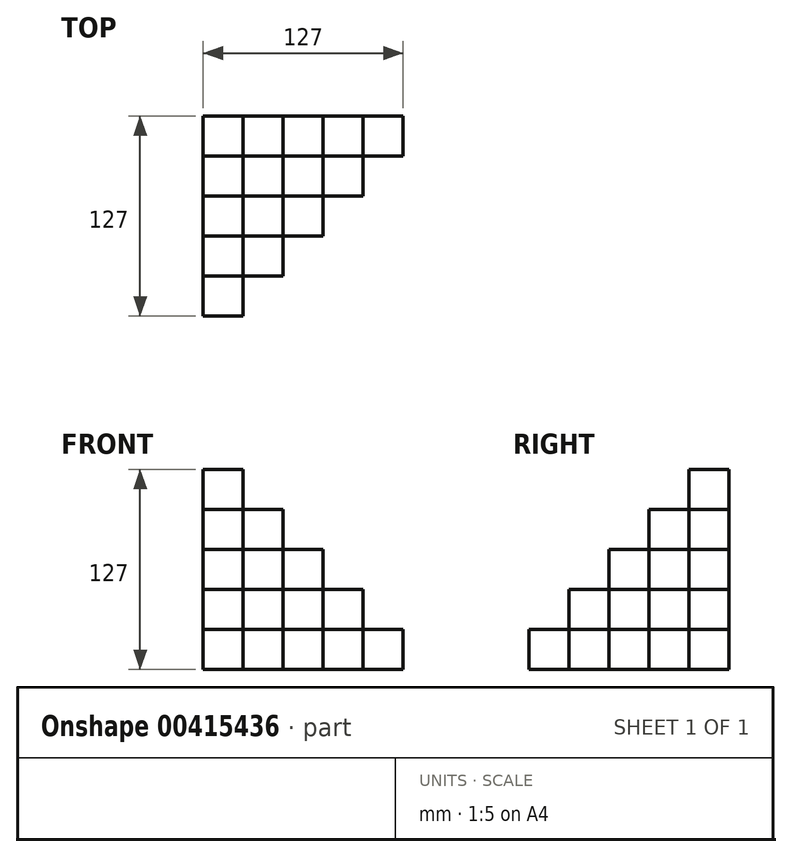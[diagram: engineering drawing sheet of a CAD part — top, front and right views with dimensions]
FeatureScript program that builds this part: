
annotation { "Feature Type Name" : "Feature", "Feature Type Description" : "" }
export const myFeature = defineFeature(function(context is Context, id is Id, definition is map)
    precondition{}
    {
        {
            var Q0;
            Q0=qCreatedBy(makeId("Top.planeOp"),FACE);
            var sketch = newSketch(context, id + "F0", { "sketchPlane" : qUnion([Q0])});
            skLineSegment(sketch, "E0.bottom", {"start": v(63.5, 63.5) * mm, "end": v(-63.5, 63.5) * mm, "construction": true});
            skLineSegment(sketch, "E0.top", {"start": v(63.5, -63.5) * mm, "end": v(-63.5, -63.5) * mm, "construction": true});
            skLineSegment(sketch, "E0.left", {"start": v(63.5, 63.5) * mm, "end": v(63.5, -63.5) * mm, "construction": true});
            skLineSegment(sketch, "E0.right", {"start": v(-63.5, 63.5) * mm, "end": v(-63.5, -63.5) * mm, "construction": true});
            skPoint(sketch, "E0.middle", {"position": v(0, 0) * mm});
            skLineSegment(sketch, "E1.bottom", {"start": v(-63.5, -63.5) * mm, "end": v(-38.1, -63.5) * mm});
            skLineSegment(sketch, "E1.top", {"start": v(-63.5, -38.1) * mm, "end": v(-38.1, -38.1) * mm});
            skLineSegment(sketch, "E1.left", {"start": v(-63.5, -63.5) * mm, "end": v(-63.5, -38.1) * mm});
            skLineSegment(sketch, "E1.right", {"start": v(-38.1, -63.5) * mm, "end": v(-38.1, -38.1) * mm});
            skLineSegment(sketch, "E2.bottom", {"start": v(-38.1, -38.1) * mm, "end": v(-12.7, -38.1) * mm});
            skLineSegment(sketch, "E2.top", {"start": v(-38.1, -12.7) * mm, "end": v(-12.7, -12.7) * mm});
            skLineSegment(sketch, "E2.left", {"start": v(-38.1, -38.1) * mm, "end": v(-38.1, -12.7) * mm});
            skLineSegment(sketch, "E2.right", {"start": v(-12.7, -38.1) * mm, "end": v(-12.7, -12.7) * mm});
            skLineSegment(sketch, "E3.bottom", {"start": v(-12.7, -12.7) * mm, "end": v(12.7, -12.7) * mm});
            skLineSegment(sketch, "E3.top", {"start": v(-12.7, 12.7) * mm, "end": v(12.7, 12.7) * mm});
            skLineSegment(sketch, "E3.left", {"start": v(-12.7, -12.7) * mm, "end": v(-12.7, 12.7) * mm});
            skLineSegment(sketch, "E3.right", {"start": v(12.7, -12.7) * mm, "end": v(12.7, 12.7) * mm});
            skLineSegment(sketch, "E4.bottom", {"start": v(12.7, 12.7) * mm, "end": v(38.1, 12.7) * mm});
            skLineSegment(sketch, "E4.top", {"start": v(12.7, 38.1) * mm, "end": v(38.1, 38.1) * mm});
            skLineSegment(sketch, "E4.left", {"start": v(12.7, 12.7) * mm, "end": v(12.7, 38.1) * mm});
            skLineSegment(sketch, "E4.right", {"start": v(38.1, 12.7) * mm, "end": v(38.1, 38.1) * mm});
            skLineSegment(sketch, "E5.bottom", {"start": v(38.1, 38.1) * mm, "end": v(63.5, 38.1) * mm});
            skLineSegment(sketch, "E5.top", {"start": v(38.1, 63.5) * mm, "end": v(63.5, 63.5) * mm});
            skLineSegment(sketch, "E5.left", {"start": v(38.1, 38.1) * mm, "end": v(38.1, 63.5) * mm});
            skLineSegment(sketch, "E5.right", {"start": v(63.5, 38.1) * mm, "end": v(63.5, 63.5) * mm});
            skSolve(sketch);
        }
        {
            var Q0;
            Q0=makeQuery(id+"F0.imprint","IMPRINT",FACE,{"disambiguationData":[TD([[makeQuery(id+"F0.imprint","IMPRINT",EDGE,{"derivedFrom":sQuery(id+"F0.wireOp",EDGE,"E2.bottom")}),1.0]])]});
            var Q1;
            Q1=makeQuery(id+"F0.imprint","IMPRINT",FACE,{"disambiguationData":[TD([[makeQuery(id+"F0.imprint","IMPRINT",EDGE,{"derivedFrom":sQuery(id+"F0.wireOp",EDGE,"E1.bottom")}),1.0]])]});
            var Q2;
            Q2=makeQuery(id+"F0.imprint","IMPRINT",FACE,{"disambiguationData":[TD([[makeQuery(id+"F0.imprint","IMPRINT",EDGE,{"derivedFrom":sQuery(id+"F0.wireOp",EDGE,"E3.bottom")}),1.0]])]});
            var Q3;
            Q3=makeQuery(id+"F0.imprint","IMPRINT",FACE,{"disambiguationData":[TD([[makeQuery(id+"F0.imprint","IMPRINT",EDGE,{"derivedFrom":sQuery(id+"F0.wireOp",EDGE,"E4.bottom")}),1.0]])]});
            var Q4;
            Q4=makeQuery(id+"F0.imprint","IMPRINT",FACE,{"disambiguationData":[TD([[makeQuery(id+"F0.imprint","IMPRINT",EDGE,{"derivedFrom":sQuery(id+"F0.wireOp",EDGE,"E5.bottom")}),1.0]])]});
            extrude(context, id + "F1", {"entities" : qUnion([Q0, Q1, Q2, Q3, Q4]), "depth" : 25.4 * mm});
        }
        {
            var Q0;
            Q0=qCreatedBy(makeId("Top.planeOp"),FACE);
            var sketch = newSketch(context, id + "F2", { "sketchPlane" : qUnion([Q0])});
            skLineSegment(sketch, "E6.bottom", {"start": v(63.5, 63.5) * mm, "end": v(-63.5, 63.5) * mm, "construction": true});
            skLineSegment(sketch, "E6.top", {"start": v(63.5, -63.5) * mm, "end": v(-63.5, -63.5) * mm, "construction": true});
            skLineSegment(sketch, "E6.left", {"start": v(63.5, 63.5) * mm, "end": v(63.5, -63.5) * mm, "construction": true});
            skLineSegment(sketch, "E6.right", {"start": v(-63.5, 63.5) * mm, "end": v(-63.5, -63.5) * mm, "construction": true});
            skPoint(sketch, "E6.middle", {"position": v(0, 0) * mm});
            skLineSegment(sketch, "E7", {"start": v(-63.5, -63.5) * mm, "end": v(-63.5, -38.1) * mm, "construction": true});
            skLineSegment(sketch, "E8", {"start": v(63.5, 63.5) * mm, "end": v(38.1, 63.5) * mm, "construction": true});
            skLineSegment(sketch, "E9.bottom", {"start": v(-63.5, -38.1) * mm, "end": v(-38.1, -38.1) * mm});
            skLineSegment(sketch, "E9.top", {"start": v(-63.5, -12.7) * mm, "end": v(-38.1, -12.7) * mm});
            skLineSegment(sketch, "E9.left", {"start": v(-63.5, -38.1) * mm, "end": v(-63.5, -12.7) * mm});
            skLineSegment(sketch, "E9.right", {"start": v(-38.1, -38.1) * mm, "end": v(-38.1, -12.7) * mm});
            skLineSegment(sketch, "E10.bottom", {"start": v(-38.1, -12.7) * mm, "end": v(-12.7, -12.7) * mm});
            skLineSegment(sketch, "E10.top", {"start": v(-38.1, 12.7) * mm, "end": v(-12.7, 12.7) * mm});
            skLineSegment(sketch, "E10.left", {"start": v(-38.1, -12.7) * mm, "end": v(-38.1, 12.7) * mm});
            skLineSegment(sketch, "E10.right", {"start": v(-12.7, -12.7) * mm, "end": v(-12.7, 12.7) * mm});
            skLineSegment(sketch, "E11.bottom", {"start": v(-12.7, 12.7) * mm, "end": v(12.7, 12.7) * mm});
            skLineSegment(sketch, "E11.top", {"start": v(-12.7, 38.1) * mm, "end": v(12.7, 38.1) * mm});
            skLineSegment(sketch, "E11.left", {"start": v(-12.7, 12.7) * mm, "end": v(-12.7, 38.1) * mm});
            skLineSegment(sketch, "E11.right", {"start": v(12.7, 12.7) * mm, "end": v(12.7, 38.1) * mm});
            skLineSegment(sketch, "E12.bottom", {"start": v(12.7, 38.1) * mm, "end": v(38.1, 38.1) * mm});
            skLineSegment(sketch, "E12.top", {"start": v(12.7, 63.5) * mm, "end": v(38.1, 63.5) * mm});
            skLineSegment(sketch, "E12.left", {"start": v(12.7, 38.1) * mm, "end": v(12.7, 63.5) * mm});
            skLineSegment(sketch, "E12.right", {"start": v(38.1, 38.1) * mm, "end": v(38.1, 63.5) * mm});
            skSolve(sketch);
        }
        {
            var Q0;
            Q0 = qSketchRegion(id + "F2", true);
            extrude(context, id + "F3", {"entities" : qUnion([Q0]), "depth" : 50.8 * mm});
        }
        {
            var Q0;
            Q0=qCreatedBy(makeId("Top.planeOp"),FACE);
            var sketch = newSketch(context, id + "F4", { "sketchPlane" : qUnion([Q0])});
            skLineSegment(sketch, "E13.bottom", {"start": v(63.5, 63.5) * mm, "end": v(-63.5, 63.5) * mm, "construction": true});
            skLineSegment(sketch, "E13.top", {"start": v(63.5, -63.5) * mm, "end": v(-63.5, -63.5) * mm, "construction": true});
            skLineSegment(sketch, "E13.left", {"start": v(63.5, 63.5) * mm, "end": v(63.5, -63.5) * mm, "construction": true});
            skLineSegment(sketch, "E13.right", {"start": v(-63.5, 63.5) * mm, "end": v(-63.5, -63.5) * mm, "construction": true});
            skPoint(sketch, "E13.middle", {"position": v(0, 0) * mm});
            skLineSegment(sketch, "E14", {"start": v(-63.5, -63.5) * mm, "end": v(-63.5, -12.7) * mm, "construction": true});
            skLineSegment(sketch, "E15", {"start": v(63.5, 63.5) * mm, "end": v(12.7, 63.5) * mm, "construction": true});
            skLineSegment(sketch, "E16.bottom", {"start": v(12.7, 63.5) * mm, "end": v(-12.7, 63.5) * mm});
            skLineSegment(sketch, "E16.top", {"start": v(12.7, 38.1) * mm, "end": v(-12.7, 38.1) * mm});
            skLineSegment(sketch, "E16.left", {"start": v(12.7, 63.5) * mm, "end": v(12.7, 38.1) * mm});
            skLineSegment(sketch, "E16.right", {"start": v(-12.7, 63.5) * mm, "end": v(-12.7, 38.1) * mm});
            skLineSegment(sketch, "E17.bottom", {"start": v(-12.7, 38.1) * mm, "end": v(-38.1, 38.1) * mm});
            skLineSegment(sketch, "E17.top", {"start": v(-12.7, 12.7) * mm, "end": v(-38.1, 12.7) * mm});
            skLineSegment(sketch, "E17.left", {"start": v(-12.7, 38.1) * mm, "end": v(-12.7, 12.7) * mm});
            skLineSegment(sketch, "E17.right", {"start": v(-38.1, 38.1) * mm, "end": v(-38.1, 12.7) * mm});
            skLineSegment(sketch, "E18.bottom", {"start": v(-38.1, 12.7) * mm, "end": v(-63.5, 12.7) * mm});
            skLineSegment(sketch, "E18.top", {"start": v(-38.1, -12.7) * mm, "end": v(-63.5, -12.7) * mm});
            skLineSegment(sketch, "E18.left", {"start": v(-38.1, 12.7) * mm, "end": v(-38.1, -12.7) * mm});
            skLineSegment(sketch, "E18.right", {"start": v(-63.5, 12.7) * mm, "end": v(-63.5, -12.7) * mm});
            skSolve(sketch);
        }
        {
            var Q0;
            Q0=makeQuery(id+"F4.imprint","IMPRINT",FACE,{"disambiguationData":[TD([[makeQuery(id+"F4.imprint","IMPRINT",EDGE,{"derivedFrom":sQuery(id+"F4.wireOp",EDGE,"E18.bottom")}),1.0]])]});
            var Q1;
            Q1=makeQuery(id+"F4.imprint","IMPRINT",FACE,{"disambiguationData":[TD([[makeQuery(id+"F4.imprint","IMPRINT",EDGE,{"derivedFrom":sQuery(id+"F4.wireOp",EDGE,"E17.bottom")}),1.0]])]});
            var Q2;
            Q2=makeQuery(id+"F4.imprint","IMPRINT",FACE,{"disambiguationData":[TD([[makeQuery(id+"F4.imprint","IMPRINT",EDGE,{"derivedFrom":sQuery(id+"F4.wireOp",EDGE,"E16.bottom")}),1.0]])]});
            extrude(context, id + "F5", {"entities" : qUnion([Q0, Q1, Q2]), "depth" : 76.2 * mm});
        }
        {
            var Q0;
            Q0=qCreatedBy(makeId("Top.planeOp"),FACE);
            var sketch = newSketch(context, id + "F6", { "sketchPlane" : qUnion([Q0])});
            skLineSegment(sketch, "E19.bottom", {"start": v(63.5, 63.5) * mm, "end": v(-63.5, 63.5) * mm, "construction": true});
            skLineSegment(sketch, "E19.top", {"start": v(63.5, -63.5) * mm, "end": v(-63.5, -63.5) * mm, "construction": true});
            skLineSegment(sketch, "E19.left", {"start": v(63.5, 63.5) * mm, "end": v(63.5, -63.5) * mm, "construction": true});
            skLineSegment(sketch, "E19.right", {"start": v(-63.5, 63.5) * mm, "end": v(-63.5, -63.5) * mm, "construction": true});
            skPoint(sketch, "E19.middle", {"position": v(0, 0) * mm});
            skLineSegment(sketch, "E20", {"start": v(-63.5, 63.5) * mm, "end": v(-63.5, 12.7) * mm, "construction": true});
            skLineSegment(sketch, "E21", {"start": v(-63.5, 63.5) * mm, "end": v(-12.7, 63.5) * mm, "construction": true});
            skLineSegment(sketch, "E22.bottom", {"start": v(-63.5, 12.7) * mm, "end": v(-38.1, 12.7) * mm});
            skLineSegment(sketch, "E22.top", {"start": v(-63.5, 38.1) * mm, "end": v(-38.1, 38.1) * mm});
            skLineSegment(sketch, "E22.left", {"start": v(-63.5, 12.7) * mm, "end": v(-63.5, 38.1) * mm});
            skLineSegment(sketch, "E22.right", {"start": v(-38.1, 12.7) * mm, "end": v(-38.1, 38.1) * mm});
            skLineSegment(sketch, "E23.bottom", {"start": v(-38.1, 38.1) * mm, "end": v(-12.7, 38.1) * mm});
            skLineSegment(sketch, "E23.top", {"start": v(-38.1, 63.5) * mm, "end": v(-12.7, 63.5) * mm});
            skLineSegment(sketch, "E23.left", {"start": v(-38.1, 38.1) * mm, "end": v(-38.1, 63.5) * mm});
            skLineSegment(sketch, "E23.right", {"start": v(-12.7, 38.1) * mm, "end": v(-12.7, 63.5) * mm});
            skSolve(sketch);
        }
        {
            var Q0;
            Q0=makeQuery(id+"F6.imprint","IMPRINT",FACE,{"disambiguationData":[TD([[makeQuery(id+"F6.imprint","IMPRINT",EDGE,{"derivedFrom":sQuery(id+"F6.wireOp",EDGE,"E22.bottom")}),1.0]])]});
            var Q1;
            Q1=makeQuery(id+"F6.imprint","IMPRINT",FACE,{"disambiguationData":[TD([[makeQuery(id+"F6.imprint","IMPRINT",EDGE,{"derivedFrom":sQuery(id+"F6.wireOp",EDGE,"E23.bottom")}),1.0]])]});
            extrude(context, id + "F7", {"entities" : qUnion([Q0, Q1]), "depth" : 101.6 * mm});
        }
        {
            var Q0;
            Q0=qCreatedBy(makeId("Top.planeOp"),FACE);
            var sketch = newSketch(context, id + "F8", { "sketchPlane" : qUnion([Q0])});
            skLineSegment(sketch, "E24.bottom", {"start": v(63.5, 63.5) * mm, "end": v(-63.5, 63.5) * mm, "construction": true});
            skLineSegment(sketch, "E24.top", {"start": v(63.5, -63.5) * mm, "end": v(-63.5, -63.5) * mm, "construction": true});
            skLineSegment(sketch, "E24.left", {"start": v(63.5, 63.5) * mm, "end": v(63.5, -63.5) * mm, "construction": true});
            skLineSegment(sketch, "E24.right", {"start": v(-63.5, 63.5) * mm, "end": v(-63.5, -63.5) * mm, "construction": true});
            skPoint(sketch, "E24.middle", {"position": v(0, 0) * mm});
            skLineSegment(sketch, "E25.bottom", {"start": v(-63.5, 63.5) * mm, "end": v(-38.1, 63.5) * mm});
            skLineSegment(sketch, "E25.top", {"start": v(-63.5, 38.1) * mm, "end": v(-38.1, 38.1) * mm});
            skLineSegment(sketch, "E25.left", {"start": v(-63.5, 63.5) * mm, "end": v(-63.5, 38.1) * mm});
            skLineSegment(sketch, "E25.right", {"start": v(-38.1, 63.5) * mm, "end": v(-38.1, 38.1) * mm});
            skSolve(sketch);
        }
        {
            var Q0;
            Q0=makeQuery(id+"F8.imprint","IMPRINT",FACE,{"disambiguationData":[TD([[makeQuery(id+"F8.imprint","IMPRINT",EDGE,{"derivedFrom":sQuery(id+"F8.wireOp",EDGE,"E25.bottom")}),-1.0]])]});
            extrude(context, id + "F9", {"entities" : qUnion([Q0]), "depth" : 127 * mm});
        }
    });
